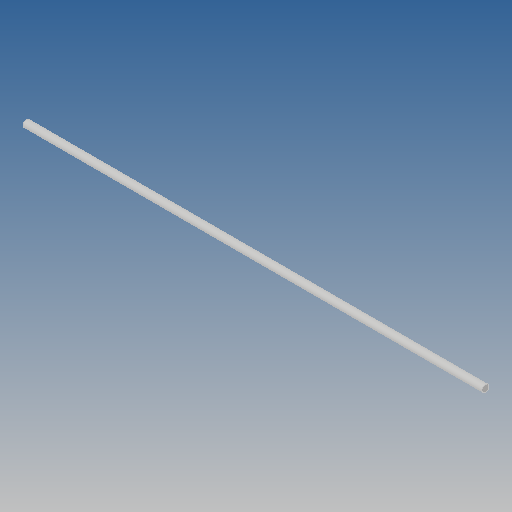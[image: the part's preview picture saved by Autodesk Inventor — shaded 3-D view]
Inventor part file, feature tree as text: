
AUTODESK INVENTOR PART (.ipt)
format: ipt  version: 2018 (Build 220112000, 112)  size: 77,824 bytes
history: native  units: mm
features: other x1, extrude x1, sketch x1
ambient origin geometry x8: Origin, YZ Plane, XZ Plane, XY Plane, X Axis, Y Axis, Z Axis, Center Point
bodies: Solid1 (feature_tree)
feature tree (3):
  other  "<userpath>\OneDrive\Objet3D\3DPrinter\Parameters.xlsx"
  extrude  "Extrusion1"  Depth=500.0mm TaperAngle=0.0deg
  sketch  "Sketch1"  dims[d0=8.0mm d1=500.0mm d2=0.0mm]
